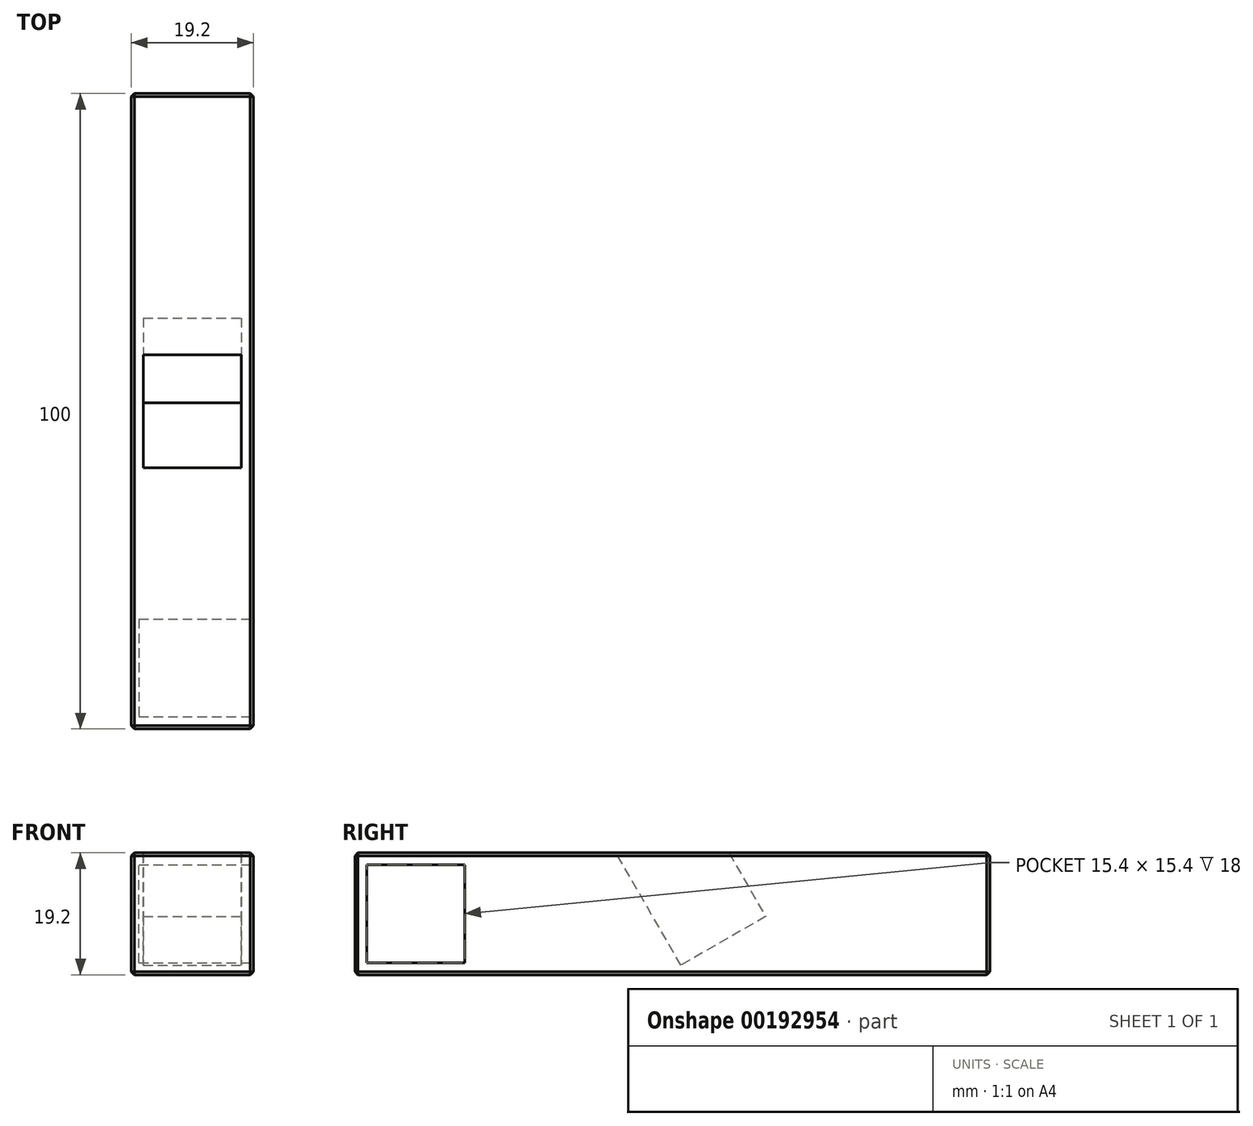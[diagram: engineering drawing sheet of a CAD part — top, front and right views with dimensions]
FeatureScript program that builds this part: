
annotation { "Feature Type Name" : "Feature", "Feature Type Description" : "" }
export const myFeature = defineFeature(function(context is Context, id is Id, definition is map)
    precondition{}
    {
        {
            var Q0;
            Q0=qCreatedBy(makeId("Top.planeOp"),FACE);
            var sketch = newSketch(context, id + "F0", { "sketchPlane" : qUnion([Q0])});
            skLineSegment(sketch, "E0.bottom", {"start": v(9.6, -50) * mm, "end": v(-9.6, -50) * mm});
            skLineSegment(sketch, "E0.top", {"start": v(9.6, 50) * mm, "end": v(-9.6, 50) * mm});
            skLineSegment(sketch, "E0.left", {"start": v(9.6, -50) * mm, "end": v(9.6, 50) * mm});
            skLineSegment(sketch, "E0.right", {"start": v(-9.6, -50) * mm, "end": v(-9.6, 50) * mm});
            skPoint(sketch, "E0.middle", {"position": v(0, 0) * mm});
            skSolve(sketch);
        }
        {
            var Q0;
            Q0=qSketchRegion(id+"F0",true);
            extrude(context, id + "F1", {"entities" : qUnion([Q0]), "depth" : 19.2 * mm});
        }
        {
            var Q0;
            Q0=makeQuery(id+"F1.opExtrude","SWEPT_FACE",FACE,{"disambiguationData":[OSD([sQuery(id+"F0.wireOp",EDGE,"E0.left")])]});
            var sketch = newSketch(context, id + "F2", { "sketchPlane" : qUnion([Q0])});
            skLineSegment(sketch, "E1.bottom", {"start": v(-32.7, 1.9) * mm, "end": v(-48.1, 1.9) * mm});
            skLineSegment(sketch, "E1.top", {"start": v(-32.7, 17.3) * mm, "end": v(-48.1, 17.3) * mm});
            skLineSegment(sketch, "E1.left", {"start": v(-32.7, 1.9) * mm, "end": v(-32.7, 17.3) * mm});
            skLineSegment(sketch, "E1.right", {"start": v(-48.1, 1.9) * mm, "end": v(-48.1, 17.3) * mm});
            skPoint(sketch, "E1.middle", {"position": v(-40.4, 9.6) * mm});
            skPoint(sketch, "E1.middle.positionSnap0", {"position": v(-50, 9.6) * mm});
            skPoint(sketch, "E1.centerSnap0", {"position": v(-50, 9.6) * mm});
            skSolve(sketch);
        }
        {
            var Q0;
            Q0=qSketchRegion(id+"F2",true);
            extrude(context, id + "F3", {"entities" : qUnion([Q0]), "operationType" : NewBodyOperationType.REMOVE, "oppositeDirection" : true, "depth" : 18 * mm});
        }
        {
            var Q0;
            Q0=qCreatedBy(makeId("Right.planeOp"),FACE);
            var sketch = newSketch(context, id + "F4", { "sketchPlane" : qUnion([Q0])});
            skPoint(sketch, "E2.0", {"position": v(0, 19.2) * mm});
            skLineSegment(sketch, "E3", {"start": v(0, 19.2) * mm, "end": v(8, 5.34) * mm});
            skLineSegment(sketch, "E4", {"start": v(8, 5.34) * mm, "end": v(1.33, 1.5) * mm});
            skLineSegment(sketch, "E5", {"start": v(1.33, 1.5) * mm, "end": v(-23.8, 45.03) * mm});
            skLineSegment(sketch, "E6", {"start": v(-23.8, 45.03) * mm, "end": v(-10.47, 52.73) * mm});
            skLineSegment(sketch, "E7", {"start": v(-10.47, 52.73) * mm, "end": v(14.67, 9.2) * mm});
            skLineSegment(sketch, "E8", {"start": v(8, 5.34) * mm, "end": v(14.67, 9.2) * mm});
            skSolve(sketch);
        }
        {
            var Q0;
            Q0 = qSketchRegion(id + "F4", true);
            extrude(context, id + "F5", {"entities" : qUnion([Q0]), "operationType" : NewBodyOperationType.REMOVE, "oppositeDirection" : true, "depth" : (15.4 / 2) * mm, "hasSecondDirection" : true, "secondDirectionOppositeDirection" : false, "secondDirectionDepth" : 7.7 * mm});
        }
        {
            var Q0;
            Q0=makeQuery(id+"F1.opExtrude","SWEPT_FACE",FACE,{"disambiguationData":[OSD([sQuery(id+"F0.wireOp",EDGE,"E0.right")])]});
            var Q1;
            Q1=makeQuery(id+"F1.opExtrude","SWEPT_FACE",FACE,{"disambiguationData":[OSD([sQuery(id+"F0.wireOp",EDGE,"E0.bottom")])]});
            var Q2;
            Q2=makeQuery(id+"F1.opExtrude","SWEPT_FACE",FACE,{"disambiguationData":[OSD([sQuery(id+"F0.wireOp",EDGE,"E0.top")])]});
            var Q3;
            Q3=makeQuery(id+"F1.opExtrude","CAP_FACE",FACE,{"disambiguationData":[OSD([sQuery(id+"F0.wireOp",EDGE,"E0.bottom"),sQuery(id+"F0.wireOp",EDGE,"E0.top"),sQuery(id+"F0.wireOp",EDGE,"E0.left"),sQuery(id+"F0.wireOp",EDGE,"E0.right")])],"isStart":true});
            var Q4;
            Q4=makeQuery(id+"F1.opExtrude","CAP_EDGE",EDGE,{"disambiguationData":[OSD([sQuery(id+"F0.wireOp",EDGE,"E0.left")])],"isStart":false});
            chamfer(context, id + "F6", {"entities" : qUnion([Q0, Q1, Q2, Q3, Q4]), "width" : 0.5 * mm, "tangentPropagation" : true});
        }
    });
